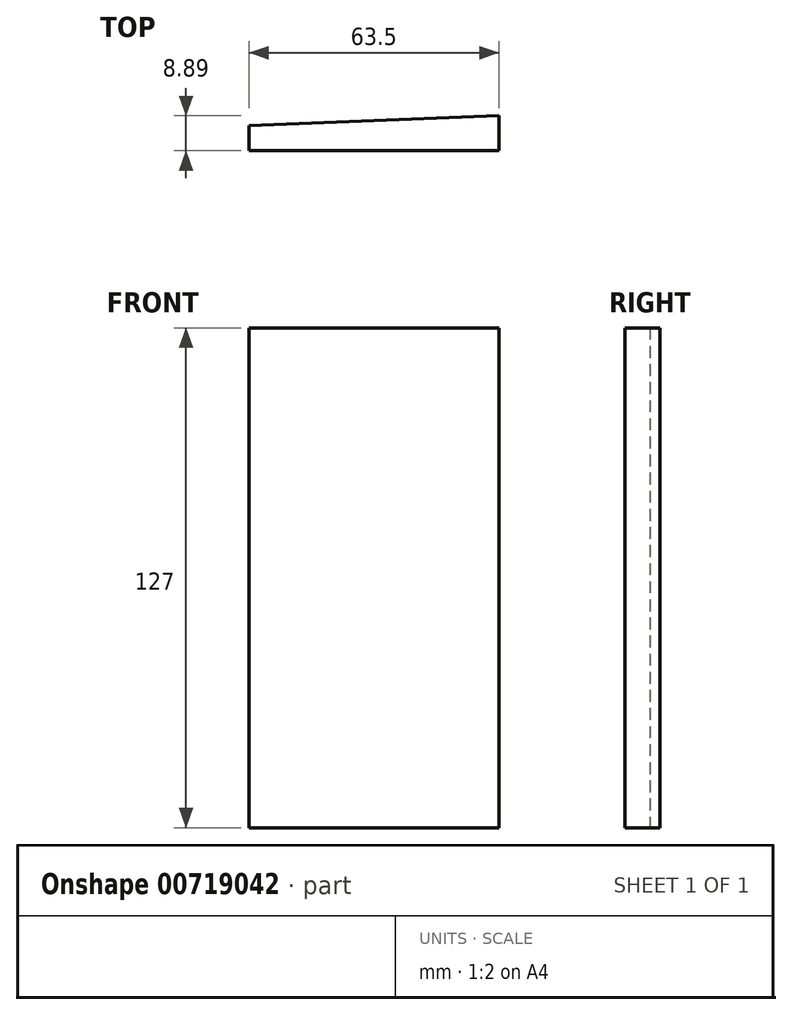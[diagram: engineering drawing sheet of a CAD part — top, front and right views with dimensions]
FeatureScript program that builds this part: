
annotation { "Feature Type Name" : "Feature", "Feature Type Description" : "" }
export const myFeature = defineFeature(function(context is Context, id is Id, definition is map)
    precondition{}
    {
        {
            var Q0;
            Q0=qCreatedBy(makeId("Top.planeOp"),FACE);
            var sketch = newSketch(context, id + "F0", { "sketchPlane" : qUnion([Q0])});
            skLineSegment(sketch, "E0", {"start": v(0, 0) * mm, "end": v(-63.5, 0) * mm});
            skLineSegment(sketch, "E1", {"start": v(-63.5, 0) * mm, "end": v(-63.5, 6.35) * mm});
            skLineSegment(sketch, "E2", {"start": v(-63.5, 6.35) * mm, "end": v(0, 8.9) * mm});
            skLineSegment(sketch, "E3", {"start": v(0, 8.9) * mm, "end": v(0, 0) * mm});
            skSolve(sketch);
        }
        {
            var Q0;
            Q0=makeQuery(id+"F0.imprint","IMPRINT",FACE,{"disambiguationData":[TD([[makeQuery(id+"F0.imprint","IMPRINT",EDGE,{"derivedFrom":sQuery(id+"F0.wireOp",EDGE,"E0")}),-1.0]])]});
            extrude(context, id + "F1", {"entities" : qUnion([Q0]), "depth" : 127 * mm, "offsetDistance" : 25.4 * mm});
        }
    });
